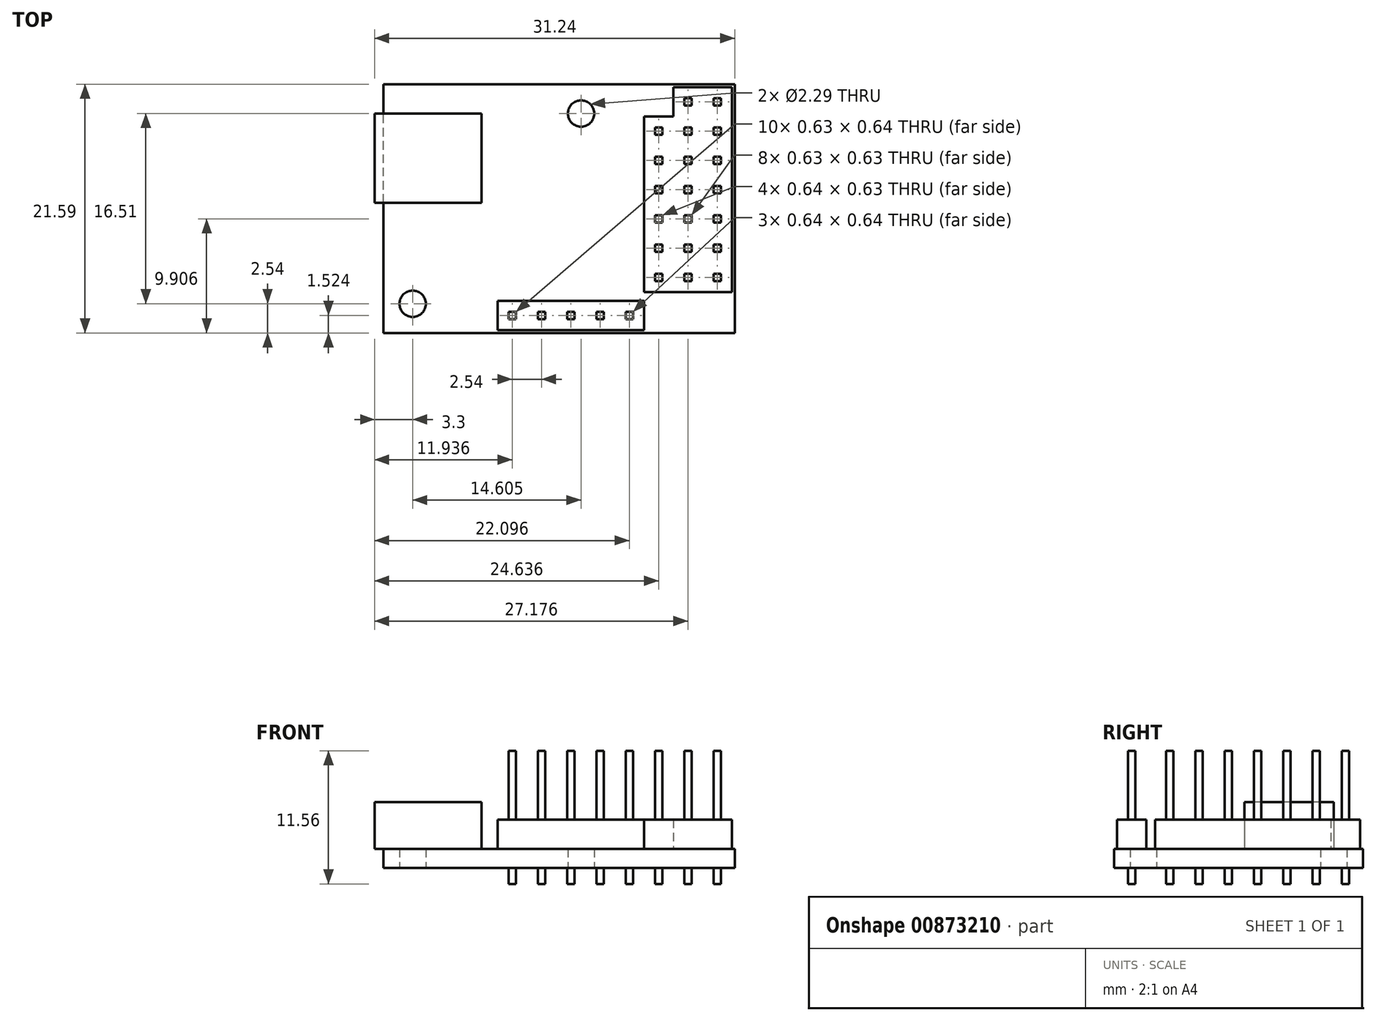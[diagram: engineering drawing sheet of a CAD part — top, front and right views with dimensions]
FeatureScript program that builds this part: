
annotation { "Feature Type Name" : "Feature", "Feature Type Description" : "" }
export const myFeature = defineFeature(function(context is Context, id is Id, definition is map)
    precondition{}
    {
        {
            var Q0;
            Q0=qCreatedBy(makeId("Top.planeOp"),FACE);
            var sketch = newSketch(context, id + "F0", { "sketchPlane" : qUnion([Q0])});
            skLineSegment(sketch, "E0.bottom", {"start": v(0, 0) * mm, "end": v(30.48, 0) * mm});
            skLineSegment(sketch, "E0.top", {"start": v(0, 21.59) * mm, "end": v(30.48, 21.59) * mm});
            skLineSegment(sketch, "E0.left", {"start": v(0, 0) * mm, "end": v(0, 21.59) * mm});
            skLineSegment(sketch, "E0.right", {"start": v(30.48, 0) * mm, "end": v(30.48, 21.6) * mm});
            skLineSegment(sketch, "E1", {"start": v(2.54, 19.05) * mm, "end": v(17.14, 19.05) * mm, "construction": true});
            skLineSegment(sketch, "E2", {"start": v(2.54, 19.05) * mm, "end": v(2.54, 2.54) * mm, "construction": true});
            skCircle(sketch, "E3", {"center": v(17.14, 19.05) * mm, "radius": 1.14 * mm});
            skCircle(sketch, "E4", {"center": v(2.54, 2.54) * mm, "radius": 1.14 * mm});
            skSolve(sketch);
        }
        {
            var Q0;
            Q0 = qSketchRegion(id + "F0", true);
            extrude(context, id + "F1", {"entities" : qUnion([Q0]), "depth" : 1.65 * mm, "offsetDistance" : 25.4 * mm});
        }
        {
            var Q0;
            Q0=makeQuery(id+"F1.opExtrude","CAP_FACE",FACE,{"disambiguationData":[OSD([sQuery(id+"F0.wireOp",EDGE,"E0.bottom"),sQuery(id+"F0.wireOp",EDGE,"E0.top"),sQuery(id+"F0.wireOp",EDGE,"E0.left"),sQuery(id+"F0.wireOp",EDGE,"E0.right"),sQuery(id+"F0.wireOp",EDGE,"E3"),sQuery(id+"F0.wireOp",EDGE,"E4")])],"isStart":false});
            var sketch = newSketch(context, id + "F2", { "sketchPlane" : qUnion([Q0])});
            skLineSegment(sketch, "E5.bottom", {"start": v(30.23, 21.34) * mm, "end": v(25.15, 21.34) * mm});
            skLineSegment(sketch, "E5.right", {"start": v(25.15, 21.34) * mm, "end": v(25.15, 18.8) * mm});
            skLineSegment(sketch, "E6.top", {"start": v(30.23, 3.56) * mm, "end": v(22.6, 3.56) * mm});
            skLineSegment(sketch, "E6.left", {"start": v(30.23, 21.34) * mm, "end": v(30.23, 3.56) * mm});
            skLineSegment(sketch, "E6.right", {"start": v(22.6, 18.8) * mm, "end": v(22.6, 3.56) * mm});
            skLineSegment(sketch, "E7.bottom", {"start": v(22.6, 2.8) * mm, "end": v(9.9, 2.8) * mm});
            skLineSegment(sketch, "E7.top", {"start": v(22.6, 0.25) * mm, "end": v(9.9, 0.25) * mm});
            skLineSegment(sketch, "E7.left", {"start": v(22.6, 2.8) * mm, "end": v(22.6, 0.25) * mm});
            skLineSegment(sketch, "E7.right", {"start": v(9.9, 2.8) * mm, "end": v(9.9, 0.25) * mm});
            skLineSegment(sketch, "E8", {"start": v(25.15, 18.8) * mm, "end": v(22.6, 18.8) * mm});
            skSolve(sketch);
        }
        {
            var Q0;
            Q0 = qSketchRegion(id + "F2", true);
            extrude(context, id + "F3", {"entities" : qUnion([Q0]), "depth" : 2.54 * mm, "offsetDistance" : 25.4 * mm});
        }
        {
            var Q0;
            Q0=makeQuery(id+"F3.opExtrude","CAP_FACE",FACE,{"disambiguationData":[OSD([sQuery(id+"F2.wireOp",EDGE,"E5.bottom"),sQuery(id+"F2.wireOp",EDGE,"E5.right"),sQuery(id+"F2.wireOp",EDGE,"E6.top"),sQuery(id+"F2.wireOp",EDGE,"E6.left"),sQuery(id+"F2.wireOp",EDGE,"E6.right"),sQuery(id+"F2.wireOp",EDGE,"E8")])],"isStart":false});
            var sketch = newSketch(context, id + "F4", { "sketchPlane" : qUnion([Q0])});
            skLineSegment(sketch, "E9", {"start": v(28.96, 21.34) * mm, "end": v(28.96, 3.56) * mm, "construction": true});
            skLineSegment(sketch, "E10", {"start": v(26.42, 21.34) * mm, "end": v(26.42, 3.56) * mm, "construction": true});
            skLineSegment(sketch, "E11", {"start": v(23.88, 18.8) * mm, "end": v(23.88, 3.56) * mm, "construction": true});
            skLineSegment(sketch, "E12", {"start": v(22.6, 1.52) * mm, "end": v(9.9, 1.52) * mm, "construction": true});
            skLineSegment(sketch, "E13", {"start": v(22.6, 4.83) * mm, "end": v(30.23, 4.83) * mm, "construction": true});
            skPoint(sketch, "E14.middle", {"position": v(28.96, 4.83) * mm});
            skLineSegment(sketch, "E15.bottom", {"start": v(24.2, 5.14) * mm, "end": v(23.56, 5.14) * mm});
            skLineSegment(sketch, "E15.top", {"start": v(24.2, 4.5) * mm, "end": v(23.56, 4.5) * mm});
            skLineSegment(sketch, "E15.left", {"start": v(24.2, 5.14) * mm, "end": v(24.2, 4.5) * mm});
            skLineSegment(sketch, "E15.right", {"start": v(23.56, 5.14) * mm, "end": v(23.56, 4.5) * mm});
            skPoint(sketch, "E15.middle", {"position": v(23.88, 4.83) * mm});
            skLineSegment(sketch, "E16.0.1.0", {"start": v(24.2, 7.05) * mm, "end": v(23.56, 7.05) * mm});
            skLineSegment(sketch, "E16.0.1.1", {"start": v(23.56, 7.68) * mm, "end": v(23.56, 7.05) * mm});
            skLineSegment(sketch, "E16.0.1.2", {"start": v(24.2, 7.68) * mm, "end": v(24.2, 7.05) * mm});
            skLineSegment(sketch, "E16.0.1.3", {"start": v(24.2, 7.68) * mm, "end": v(23.56, 7.68) * mm});
            skLineSegment(sketch, "E16.0.2.0", {"start": v(24.2, 9.59) * mm, "end": v(23.56, 9.59) * mm});
            skLineSegment(sketch, "E16.0.2.1", {"start": v(23.56, 10.22) * mm, "end": v(23.56, 9.59) * mm});
            skLineSegment(sketch, "E16.0.2.2", {"start": v(24.2, 10.22) * mm, "end": v(24.2, 9.59) * mm});
            skLineSegment(sketch, "E16.0.2.3", {"start": v(24.2, 10.22) * mm, "end": v(23.56, 10.22) * mm});
            skLineSegment(sketch, "E16.0.3.0", {"start": v(24.2, 12.13) * mm, "end": v(23.56, 12.13) * mm});
            skLineSegment(sketch, "E16.0.3.1", {"start": v(23.56, 12.76) * mm, "end": v(23.56, 12.13) * mm});
            skLineSegment(sketch, "E16.0.3.2", {"start": v(24.2, 12.76) * mm, "end": v(24.2, 12.13) * mm});
            skLineSegment(sketch, "E16.0.3.3", {"start": v(24.2, 12.76) * mm, "end": v(23.56, 12.76) * mm});
            skLineSegment(sketch, "E16.0.4.0", {"start": v(24.2, 14.67) * mm, "end": v(23.56, 14.67) * mm});
            skLineSegment(sketch, "E16.0.4.1", {"start": v(23.56, 15.3) * mm, "end": v(23.56, 14.67) * mm});
            skLineSegment(sketch, "E16.0.4.2", {"start": v(24.2, 15.3) * mm, "end": v(24.2, 14.67) * mm});
            skLineSegment(sketch, "E16.0.4.3", {"start": v(24.2, 15.3) * mm, "end": v(23.56, 15.3) * mm});
            skLineSegment(sketch, "E16.0.5.0", {"start": v(24.2, 17.2) * mm, "end": v(23.56, 17.2) * mm});
            skLineSegment(sketch, "E16.0.5.1", {"start": v(23.56, 17.84) * mm, "end": v(23.56, 17.2) * mm});
            skLineSegment(sketch, "E16.0.5.2", {"start": v(24.2, 17.84) * mm, "end": v(24.2, 17.2) * mm});
            skLineSegment(sketch, "E16.0.5.3", {"start": v(24.2, 17.84) * mm, "end": v(23.56, 17.84) * mm});
            skLineSegment(sketch, "E16.1.0.0", {"start": v(26.73, 4.5) * mm, "end": v(26.1, 4.5) * mm});
            skLineSegment(sketch, "E16.1.0.1", {"start": v(26.1, 5.14) * mm, "end": v(26.1, 4.5) * mm});
            skLineSegment(sketch, "E16.1.0.2", {"start": v(26.73, 5.14) * mm, "end": v(26.73, 4.5) * mm});
            skLineSegment(sketch, "E16.1.0.3", {"start": v(26.73, 5.14) * mm, "end": v(26.1, 5.14) * mm});
            skLineSegment(sketch, "E16.1.1.0", {"start": v(26.73, 7.05) * mm, "end": v(26.1, 7.05) * mm});
            skLineSegment(sketch, "E16.1.1.1", {"start": v(26.1, 7.68) * mm, "end": v(26.1, 7.05) * mm});
            skLineSegment(sketch, "E16.1.1.2", {"start": v(26.73, 7.68) * mm, "end": v(26.73, 7.05) * mm});
            skLineSegment(sketch, "E16.1.1.3", {"start": v(26.73, 7.68) * mm, "end": v(26.1, 7.68) * mm});
            skLineSegment(sketch, "E16.1.2.0", {"start": v(26.73, 9.59) * mm, "end": v(26.1, 9.59) * mm});
            skLineSegment(sketch, "E16.1.2.1", {"start": v(26.1, 10.22) * mm, "end": v(26.1, 9.59) * mm});
            skLineSegment(sketch, "E16.1.2.2", {"start": v(26.73, 10.22) * mm, "end": v(26.73, 9.59) * mm});
            skLineSegment(sketch, "E16.1.2.3", {"start": v(26.73, 10.22) * mm, "end": v(26.1, 10.22) * mm});
            skLineSegment(sketch, "E16.1.3.0", {"start": v(26.73, 12.13) * mm, "end": v(26.1, 12.13) * mm});
            skLineSegment(sketch, "E16.1.3.1", {"start": v(26.1, 12.76) * mm, "end": v(26.1, 12.13) * mm});
            skLineSegment(sketch, "E16.1.3.2", {"start": v(26.73, 12.76) * mm, "end": v(26.73, 12.13) * mm});
            skLineSegment(sketch, "E16.1.3.3", {"start": v(26.73, 12.76) * mm, "end": v(26.1, 12.76) * mm});
            skLineSegment(sketch, "E16.1.4.0", {"start": v(26.73, 14.67) * mm, "end": v(26.1, 14.67) * mm});
            skLineSegment(sketch, "E16.1.4.1", {"start": v(26.1, 15.3) * mm, "end": v(26.1, 14.67) * mm});
            skLineSegment(sketch, "E16.1.4.2", {"start": v(26.73, 15.3) * mm, "end": v(26.73, 14.67) * mm});
            skLineSegment(sketch, "E16.1.4.3", {"start": v(26.73, 15.3) * mm, "end": v(26.1, 15.3) * mm});
            skLineSegment(sketch, "E16.1.5.0", {"start": v(26.73, 17.2) * mm, "end": v(26.1, 17.2) * mm});
            skLineSegment(sketch, "E16.1.5.1", {"start": v(26.1, 17.84) * mm, "end": v(26.1, 17.2) * mm});
            skLineSegment(sketch, "E16.1.5.2", {"start": v(26.73, 17.84) * mm, "end": v(26.73, 17.2) * mm});
            skLineSegment(sketch, "E16.1.5.3", {"start": v(26.73, 17.84) * mm, "end": v(26.1, 17.84) * mm});
            skLineSegment(sketch, "E16.1.6.0", {"start": v(26.73, 19.75) * mm, "end": v(26.1, 19.75) * mm});
            skLineSegment(sketch, "E16.1.6.1", {"start": v(26.1, 20.38) * mm, "end": v(26.1, 19.75) * mm});
            skLineSegment(sketch, "E16.1.6.2", {"start": v(26.73, 20.38) * mm, "end": v(26.73, 19.75) * mm});
            skLineSegment(sketch, "E16.1.6.3", {"start": v(26.73, 20.38) * mm, "end": v(26.1, 20.38) * mm});
            skLineSegment(sketch, "E16.2.0.0", {"start": v(29.27, 4.5) * mm, "end": v(28.64, 4.5) * mm});
            skLineSegment(sketch, "E16.2.0.1", {"start": v(28.64, 5.14) * mm, "end": v(28.64, 4.5) * mm});
            skLineSegment(sketch, "E16.2.0.2", {"start": v(29.27, 5.14) * mm, "end": v(29.27, 4.5) * mm});
            skLineSegment(sketch, "E16.2.0.3", {"start": v(29.27, 5.14) * mm, "end": v(28.64, 5.14) * mm});
            skLineSegment(sketch, "E16.2.1.0", {"start": v(29.27, 7.05) * mm, "end": v(28.64, 7.05) * mm});
            skLineSegment(sketch, "E16.2.1.1", {"start": v(28.64, 7.68) * mm, "end": v(28.64, 7.05) * mm});
            skLineSegment(sketch, "E16.2.1.2", {"start": v(29.27, 7.68) * mm, "end": v(29.27, 7.05) * mm});
            skLineSegment(sketch, "E16.2.1.3", {"start": v(29.27, 7.68) * mm, "end": v(28.64, 7.68) * mm});
            skLineSegment(sketch, "E16.2.2.0", {"start": v(29.27, 9.59) * mm, "end": v(28.64, 9.59) * mm});
            skLineSegment(sketch, "E16.2.2.1", {"start": v(28.64, 10.22) * mm, "end": v(28.64, 9.59) * mm});
            skLineSegment(sketch, "E16.2.2.2", {"start": v(29.27, 10.22) * mm, "end": v(29.27, 9.59) * mm});
            skLineSegment(sketch, "E16.2.2.3", {"start": v(29.27, 10.22) * mm, "end": v(28.64, 10.22) * mm});
            skLineSegment(sketch, "E16.2.3.0", {"start": v(29.27, 12.13) * mm, "end": v(28.64, 12.13) * mm});
            skLineSegment(sketch, "E16.2.3.1", {"start": v(28.64, 12.76) * mm, "end": v(28.64, 12.13) * mm});
            skLineSegment(sketch, "E16.2.3.2", {"start": v(29.27, 12.76) * mm, "end": v(29.27, 12.13) * mm});
            skLineSegment(sketch, "E16.2.3.3", {"start": v(29.27, 12.76) * mm, "end": v(28.64, 12.76) * mm});
            skLineSegment(sketch, "E16.2.4.0", {"start": v(29.27, 14.67) * mm, "end": v(28.64, 14.67) * mm});
            skLineSegment(sketch, "E16.2.4.1", {"start": v(28.64, 15.3) * mm, "end": v(28.64, 14.67) * mm});
            skLineSegment(sketch, "E16.2.4.2", {"start": v(29.27, 15.3) * mm, "end": v(29.27, 14.67) * mm});
            skLineSegment(sketch, "E16.2.4.3", {"start": v(29.27, 15.3) * mm, "end": v(28.64, 15.3) * mm});
            skLineSegment(sketch, "E16.2.5.0", {"start": v(29.27, 17.2) * mm, "end": v(28.64, 17.2) * mm});
            skLineSegment(sketch, "E16.2.5.1", {"start": v(28.64, 17.84) * mm, "end": v(28.64, 17.2) * mm});
            skLineSegment(sketch, "E16.2.5.2", {"start": v(29.27, 17.84) * mm, "end": v(29.27, 17.2) * mm});
            skLineSegment(sketch, "E16.2.5.3", {"start": v(29.27, 17.84) * mm, "end": v(28.64, 17.84) * mm});
            skLineSegment(sketch, "E16.2.6.0", {"start": v(29.27, 19.75) * mm, "end": v(28.64, 19.75) * mm});
            skLineSegment(sketch, "E16.2.6.1", {"start": v(28.64, 20.38) * mm, "end": v(28.64, 19.75) * mm});
            skLineSegment(sketch, "E16.2.6.2", {"start": v(29.27, 20.38) * mm, "end": v(29.27, 19.75) * mm});
            skLineSegment(sketch, "E16.2.6.3", {"start": v(29.27, 20.38) * mm, "end": v(28.64, 20.38) * mm});
            skLineSegment(sketch, "E16.direction1", {"start": v(23.56, 4.5) * mm, "end": v(26.1, 4.5) * mm, "construction": true});
            skLineSegment(sketch, "E16.direction2", {"start": v(23.56, 4.5) * mm, "end": v(23.56, 7.05) * mm, "construction": true});
            skLineSegment(sketch, "E17.bottom", {"start": v(21.65, 1.84) * mm, "end": v(21.02, 1.84) * mm});
            skLineSegment(sketch, "E17.top", {"start": v(21.65, 1.2) * mm, "end": v(21.02, 1.2) * mm});
            skLineSegment(sketch, "E17.left", {"start": v(21.65, 1.84) * mm, "end": v(21.65, 1.2) * mm});
            skLineSegment(sketch, "E17.right", {"start": v(21.02, 1.84) * mm, "end": v(21.02, 1.2) * mm});
            skPoint(sketch, "E17.middle", {"position": v(21.34, 1.52) * mm});
            skLineSegment(sketch, "E18.1.0.0", {"start": v(19.11, 1.84) * mm, "end": v(18.48, 1.84) * mm});
            skLineSegment(sketch, "E18.1.0.1", {"start": v(19.11, 1.84) * mm, "end": v(19.11, 1.2) * mm});
            skLineSegment(sketch, "E18.1.0.2", {"start": v(19.11, 1.2) * mm, "end": v(18.48, 1.2) * mm});
            skLineSegment(sketch, "E18.1.0.3", {"start": v(18.48, 1.84) * mm, "end": v(18.48, 1.2) * mm});
            skLineSegment(sketch, "E18.2.0.0", {"start": v(16.57, 1.84) * mm, "end": v(15.94, 1.84) * mm});
            skLineSegment(sketch, "E18.2.0.1", {"start": v(16.57, 1.84) * mm, "end": v(16.57, 1.2) * mm});
            skLineSegment(sketch, "E18.2.0.2", {"start": v(16.57, 1.2) * mm, "end": v(15.94, 1.2) * mm});
            skLineSegment(sketch, "E18.2.0.3", {"start": v(15.94, 1.84) * mm, "end": v(15.94, 1.2) * mm});
            skLineSegment(sketch, "E18.3.0.0", {"start": v(14.03, 1.84) * mm, "end": v(13.4, 1.84) * mm});
            skLineSegment(sketch, "E18.3.0.1", {"start": v(14.03, 1.84) * mm, "end": v(14.03, 1.2) * mm});
            skLineSegment(sketch, "E18.3.0.2", {"start": v(14.03, 1.2) * mm, "end": v(13.4, 1.2) * mm});
            skLineSegment(sketch, "E18.3.0.3", {"start": v(13.4, 1.84) * mm, "end": v(13.4, 1.2) * mm});
            skLineSegment(sketch, "E18.4.0.0", {"start": v(11.5, 1.84) * mm, "end": v(10.86, 1.84) * mm});
            skLineSegment(sketch, "E18.4.0.1", {"start": v(11.5, 1.84) * mm, "end": v(11.5, 1.2) * mm});
            skLineSegment(sketch, "E18.4.0.2", {"start": v(11.5, 1.2) * mm, "end": v(10.86, 1.2) * mm});
            skLineSegment(sketch, "E18.4.0.3", {"start": v(10.86, 1.84) * mm, "end": v(10.86, 1.2) * mm});
            skLineSegment(sketch, "E18.direction1", {"start": v(21.02, 1.84) * mm, "end": v(18.48, 1.84) * mm, "construction": true});
            skSolve(sketch);
        }
        {
            var Q0;
            Q0=makeQuery(id+"F4.imprint","IMPRINT",FACE,{"disambiguationData":[TD([[makeQuery(id+"F4.imprint","IMPRINT",EDGE,{"derivedFrom":sQuery(id+"F4.wireOp",EDGE,"E17.bottom")}),1.0]])]});
            var Q1;
            Q1=makeQuery(id+"F4.imprint","IMPRINT",FACE,{"disambiguationData":[TD([[makeQuery(id+"F4.imprint","IMPRINT",EDGE,{"derivedFrom":sQuery(id+"F4.wireOp",EDGE,"E18.1.0.0")}),1.0]])]});
            var Q2;
            Q2=makeQuery(id+"F4.imprint","IMPRINT",FACE,{"disambiguationData":[TD([[makeQuery(id+"F4.imprint","IMPRINT",EDGE,{"derivedFrom":sQuery(id+"F4.wireOp",EDGE,"E18.2.0.0")}),1.0]])]});
            var Q3;
            Q3=makeQuery(id+"F4.imprint","IMPRINT",FACE,{"disambiguationData":[TD([[makeQuery(id+"F4.imprint","IMPRINT",EDGE,{"derivedFrom":sQuery(id+"F4.wireOp",EDGE,"E18.3.0.0")}),1.0]])]});
            var Q4;
            Q4=makeQuery(id+"F4.imprint","IMPRINT",FACE,{"disambiguationData":[TD([[makeQuery(id+"F4.imprint","IMPRINT",EDGE,{"derivedFrom":sQuery(id+"F4.wireOp",EDGE,"E18.4.0.0")}),1.0]])]});
            extrude(context, id + "F5", {"entities" : qUnion([Q0, Q1, Q2, Q3, Q4]), "operationType" : NewBodyOperationType.ADD, "depth" : 5.97 * mm, "offsetDistance" : 25.4 * mm, "hasSecondDirection" : true, "secondDirectionOppositeDirection" : true, "secondDirectionDepth" : 5.6 * mm});
        }
        {
            var Q0;
            Q0=makeQuery(id+"F4.imprint","IMPRINT",FACE,{"disambiguationData":[TD([[makeQuery(id+"F4.imprint","IMPRINT",EDGE,{"derivedFrom":sQuery(id+"F4.wireOp",EDGE,"E16.0.2.0")}),-1.0]])]});
            var Q1;
            Q1=makeQuery(id+"F4.imprint","IMPRINT",FACE,{"disambiguationData":[TD([[makeQuery(id+"F4.imprint","IMPRINT",EDGE,{"derivedFrom":sQuery(id+"F4.wireOp",EDGE,"E16.2.1.0")}),-1.0]])]});
            var Q2;
            Q2=makeQuery(id+"F4.imprint","IMPRINT",FACE,{"disambiguationData":[TD([[makeQuery(id+"F4.imprint","IMPRINT",EDGE,{"derivedFrom":sQuery(id+"F4.wireOp",EDGE,"E16.1.4.0")}),-1.0]])]});
            var Q3;
            Q3=makeQuery(id+"F4.imprint","IMPRINT",FACE,{"disambiguationData":[TD([[makeQuery(id+"F4.imprint","IMPRINT",EDGE,{"derivedFrom":sQuery(id+"F4.wireOp",EDGE,"E16.1.2.0")}),-1.0]])]});
            var Q4;
            Q4=makeQuery(id+"F4.imprint","IMPRINT",FACE,{"disambiguationData":[TD([[makeQuery(id+"F4.imprint","IMPRINT",EDGE,{"derivedFrom":sQuery(id+"F4.wireOp",EDGE,"E16.1.5.0")}),-1.0]])]});
            var Q5;
            Q5=makeQuery(id+"F4.imprint","IMPRINT",FACE,{"disambiguationData":[TD([[makeQuery(id+"F4.imprint","IMPRINT",EDGE,{"derivedFrom":sQuery(id+"F4.wireOp",EDGE,"E16.1.3.0")}),-1.0]])]});
            var Q6;
            Q6=makeQuery(id+"F4.imprint","IMPRINT",FACE,{"disambiguationData":[TD([[makeQuery(id+"F4.imprint","IMPRINT",EDGE,{"derivedFrom":sQuery(id+"F4.wireOp",EDGE,"E16.1.0.0")}),-1.0]])]});
            var Q7;
            Q7=makeQuery(id+"F4.imprint","IMPRINT",FACE,{"disambiguationData":[TD([[makeQuery(id+"F4.imprint","IMPRINT",EDGE,{"derivedFrom":sQuery(id+"F4.wireOp",EDGE,"E16.1.1.0")}),-1.0]])]});
            var Q8;
            Q8=makeQuery(id+"F4.imprint","IMPRINT",FACE,{"disambiguationData":[TD([[makeQuery(id+"F4.imprint","IMPRINT",EDGE,{"derivedFrom":sQuery(id+"F4.wireOp",EDGE,"E16.2.5.0")}),-1.0]])]});
            var Q9;
            Q9=makeQuery(id+"F4.imprint","IMPRINT",FACE,{"disambiguationData":[TD([[makeQuery(id+"F4.imprint","IMPRINT",EDGE,{"derivedFrom":sQuery(id+"F4.wireOp",EDGE,"E16.0.5.0")}),-1.0]])]});
            var Q10;
            Q10=makeQuery(id+"F4.imprint","IMPRINT",FACE,{"disambiguationData":[TD([[makeQuery(id+"F4.imprint","IMPRINT",EDGE,{"derivedFrom":sQuery(id+"F4.wireOp",EDGE,"E16.0.1.0")}),-1.0]])]});
            var Q11;
            Q11=makeQuery(id+"F4.imprint","IMPRINT",FACE,{"disambiguationData":[TD([[makeQuery(id+"F4.imprint","IMPRINT",EDGE,{"derivedFrom":sQuery(id+"F4.wireOp",EDGE,"E15.bottom")}),1.0]])]});
            var Q12;
            Q12=makeQuery(id+"F4.imprint","IMPRINT",FACE,{"disambiguationData":[TD([[makeQuery(id+"F4.imprint","IMPRINT",EDGE,{"derivedFrom":sQuery(id+"F4.wireOp",EDGE,"E16.2.3.0")}),-1.0]])]});
            var Q13;
            Q13=makeQuery(id+"F4.imprint","IMPRINT",FACE,{"disambiguationData":[TD([[makeQuery(id+"F4.imprint","IMPRINT",EDGE,{"derivedFrom":sQuery(id+"F4.wireOp",EDGE,"E16.0.4.0")}),-1.0]])]});
            var Q14;
            Q14=makeQuery(id+"F4.imprint","IMPRINT",FACE,{"disambiguationData":[TD([[makeQuery(id+"F4.imprint","IMPRINT",EDGE,{"derivedFrom":sQuery(id+"F4.wireOp",EDGE,"E16.0.3.0")}),-1.0]])]});
            var Q15;
            Q15=makeQuery(id+"F4.imprint","IMPRINT",FACE,{"disambiguationData":[TD([[makeQuery(id+"F4.imprint","IMPRINT",EDGE,{"derivedFrom":sQuery(id+"F4.wireOp",EDGE,"E16.2.2.0")}),-1.0]])]});
            var Q16;
            Q16=makeQuery(id+"F4.imprint","IMPRINT",FACE,{"disambiguationData":[TD([[makeQuery(id+"F4.imprint","IMPRINT",EDGE,{"derivedFrom":sQuery(id+"F4.wireOp",EDGE,"E16.2.4.0")}),-1.0]])]});
            var Q17;
            Q17=makeQuery(id+"F4.imprint","IMPRINT",FACE,{"disambiguationData":[TD([[makeQuery(id+"F4.imprint","IMPRINT",EDGE,{"derivedFrom":sQuery(id+"F4.wireOp",EDGE,"E16.2.0.0")}),-1.0]])]});
            var Q18;
            Q18=makeQuery(id+"F4.imprint","IMPRINT",FACE,{"disambiguationData":[TD([[makeQuery(id+"F4.imprint","IMPRINT",EDGE,{"derivedFrom":sQuery(id+"F4.wireOp",EDGE,"E16.2.6.0")}),-1.0]])]});
            var Q19;
            Q19=makeQuery(id+"F4.imprint","IMPRINT",FACE,{"disambiguationData":[TD([[makeQuery(id+"F4.imprint","IMPRINT",EDGE,{"derivedFrom":sQuery(id+"F4.wireOp",EDGE,"E16.1.6.0")}),-1.0]])]});
            extrude(context, id + "F6", {"entities" : qUnion([Q0, Q1, Q2, Q3, Q4, Q5, Q6, Q7, Q8, Q9, Q10, Q11, Q12, Q13, Q14, Q15, Q16, Q17, Q18, Q19]), "operationType" : NewBodyOperationType.ADD, "depth" : 5.97 * mm, "offsetDistance" : 25.4 * mm, "hasSecondDirection" : true, "secondDirectionOppositeDirection" : true, "secondDirectionDepth" : 5.6 * mm});
        }
        {
            var Q0;
            Q0=makeQuery(id+"F1.opExtrude","CAP_FACE",FACE,{"disambiguationData":[OSD([sQuery(id+"F0.wireOp",EDGE,"E0.bottom"),sQuery(id+"F0.wireOp",EDGE,"E0.top"),sQuery(id+"F0.wireOp",EDGE,"E0.left"),sQuery(id+"F0.wireOp",EDGE,"E0.right"),sQuery(id+"F0.wireOp",EDGE,"E3"),sQuery(id+"F0.wireOp",EDGE,"E4")])],"isStart":false});
            var sketch = newSketch(context, id + "F7", { "sketchPlane" : qUnion([Q0])});
            skLineSegment(sketch, "E19.bottom", {"start": v(-0.76, 19.05) * mm, "end": v(8.5, 19.05) * mm});
            skLineSegment(sketch, "E19.top", {"start": v(-0.76, 11.3) * mm, "end": v(8.5, 11.3) * mm});
            skLineSegment(sketch, "E19.left", {"start": v(-0.76, 19.05) * mm, "end": v(-0.76, 11.3) * mm});
            skLineSegment(sketch, "E19.right", {"start": v(8.5, 19.05) * mm, "end": v(8.5, 11.3) * mm});
            skSolve(sketch);
        }
        {
            var Q0;
            Q0 = qSketchRegion(id + "F7", true);
            extrude(context, id + "F8", {"entities" : qUnion([Q0]), "depth" : 4.06 * mm, "offsetDistance" : 25.4 * mm});
        }
    });
